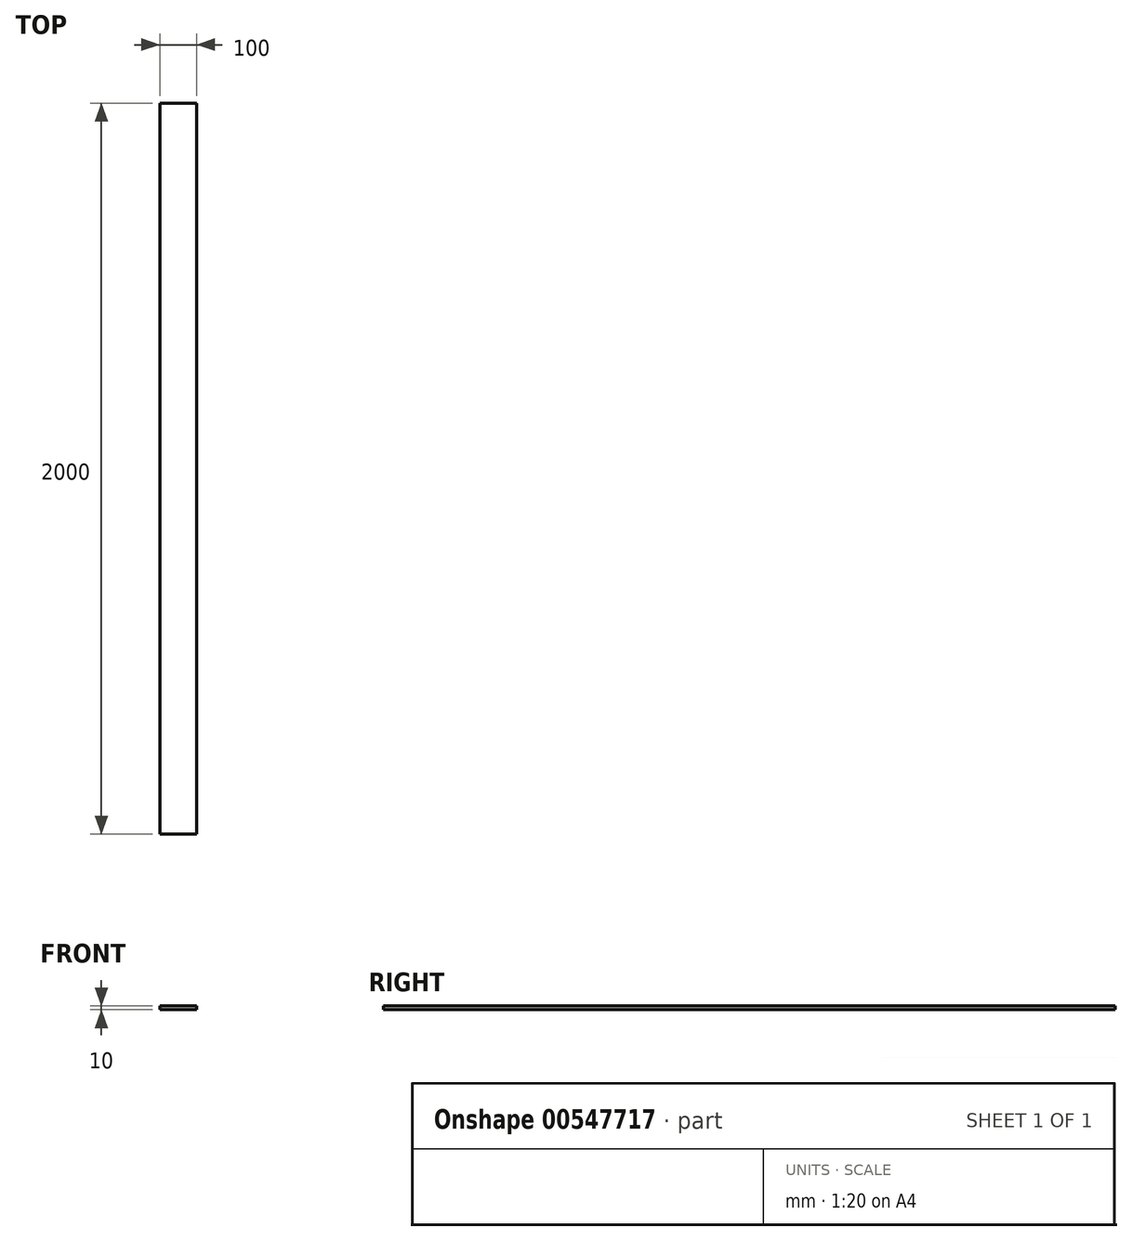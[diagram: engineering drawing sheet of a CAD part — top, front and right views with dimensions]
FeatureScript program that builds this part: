
annotation { "Feature Type Name" : "Feature", "Feature Type Description" : "" }
export const myFeature = defineFeature(function(context is Context, id is Id, definition is map)
    precondition{}
    {
        {
            var Q0;
            Q0=qCreatedBy(makeId("Front.planeOp"),FACE);
            var sketch = newSketch(context, id + "F0", { "sketchPlane" : qUnion([Q0])});
            skLineSegment(sketch, "E0.bottom", {"start": v(50, 5) * mm, "end": v(-50, 5) * mm});
            skLineSegment(sketch, "E0.top", {"start": v(50, -5) * mm, "end": v(-50, -5) * mm});
            skLineSegment(sketch, "E0.left", {"start": v(50, 5) * mm, "end": v(50, -5) * mm});
            skLineSegment(sketch, "E0.right", {"start": v(-50, 5) * mm, "end": v(-50, -5) * mm});
            skPoint(sketch, "E0.middle", {"position": v(0, 0) * mm});
            skSolve(sketch);
        }
        {
            var Q0;
            Q0 = qSketchRegion(id + "F0", true);
            extrude(context, id + "F1", {"entities" : qUnion([Q0]), "endBound" : BoundingType.SYMMETRIC, "depth" : 2000 * mm, "offsetDistance" : 25 * mm});
        }
    });
